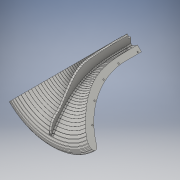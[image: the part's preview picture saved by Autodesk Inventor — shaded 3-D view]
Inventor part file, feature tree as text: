
AUTODESK INVENTOR PART (.ipt)
format: ipt  version: 2016 SP1 (Build 200210100, 210)  size: 3,705,856 bytes
history: native  units: in
note: dims shown in document units (in); Inventor stores cm internally (conversion verified against a paired STEP export)
features: hole x1, sketch x1, other x1
ambient origin geometry x8: Origin, YZ Plane, XZ Plane, XY Plane, X Axis, Y Axis, Z Axis, Center Point
bodies: Solid1 (feature_tree)
feature tree (3):
  hole  "Hole1"  [1 undecoded]
  sketch  "Sketch1"  dims[d0=0.516in d1=0.171in d2=0.432in d3=0.375in d4=0.25in d5=0.5635in d6=0.64in d7=0.8108in]
  parser-record x1  (decoder bookkeeping rows leaked as tree rows — omitted from the tree; the rows remain in map.json)
note: 1 required parameter value undecoded (feature->parameter linkage not recoverable at this tier; creation-order binding heuristic only, values carry confidence <= 0.55)
